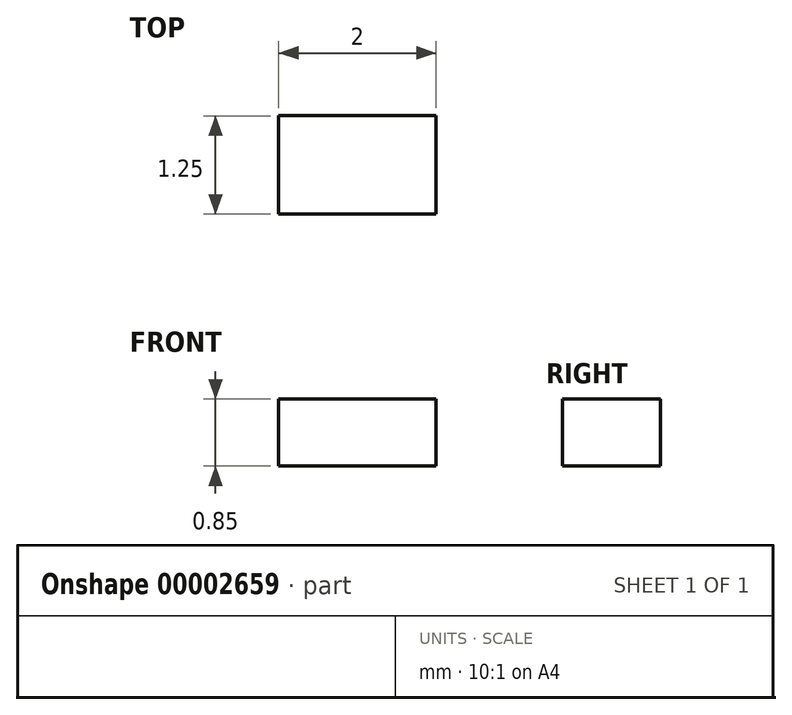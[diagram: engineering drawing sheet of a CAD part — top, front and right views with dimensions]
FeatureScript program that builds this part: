
annotation { "Feature Type Name" : "Feature", "Feature Type Description" : "" }
export const myFeature = defineFeature(function(context is Context, id is Id, definition is map)
    precondition{}
    {
        {
            var Q0;
            Q0=qCreatedBy(makeId("Top.planeOp"),FACE);
            var sketch = newSketch(context, id + "F0", { "sketchPlane" : qUnion([Q0])});
            skLineSegment(sketch, "E0.bottom", {"start": v(-0.05, 2.55) * mm, "end": v(1.95, 2.55) * mm});
            skLineSegment(sketch, "E0.top", {"start": v(-0.05, 1.3) * mm, "end": v(1.95, 1.3) * mm});
            skLineSegment(sketch, "E0.left", {"start": v(-0.05, 2.55) * mm, "end": v(-0.05, 1.3) * mm});
            skLineSegment(sketch, "E0.right", {"start": v(1.95, 2.55) * mm, "end": v(1.95, 1.3) * mm});
            skSolve(sketch);
        }
        {
            var Q0;
            Q0=makeQuery(id+"F0.imprint","IMPRINT",FACE,{"disambiguationData":[TD([[makeQuery(id+"F0.imprint","IMPRINT",EDGE,{"derivedFrom":sQuery(id+"F0.wireOp",EDGE,"E0.bottom")}),-1.0]])]});
            extrude(context, id + "F1", {"entities" : qUnion([Q0]), "depth" : .85 * mm});
        }
    });
